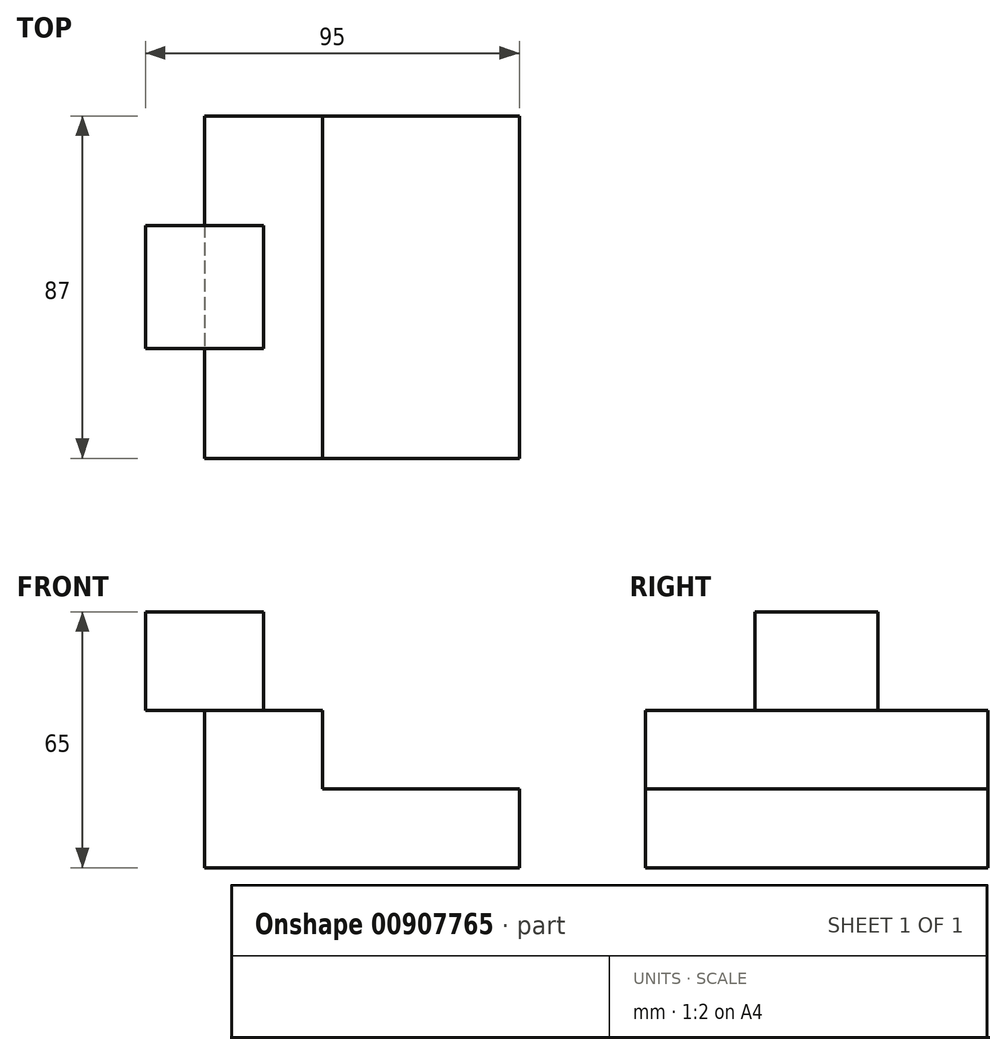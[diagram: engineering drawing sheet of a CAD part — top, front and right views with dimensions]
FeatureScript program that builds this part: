
annotation { "Feature Type Name" : "Feature", "Feature Type Description" : "" }
export const myFeature = defineFeature(function(context is Context, id is Id, definition is map)
    precondition{}
    {
        {
            var Q0;
            Q0=qCreatedBy(makeId("Front.planeOp"),FACE);
            var sketch = newSketch(context, id + "F0", { "sketchPlane" : qUnion([Q0])});
            skLineSegment(sketch, "E0.top", {"start": v(0, 40) * mm, "end": v(30, 40) * mm});
            skLineSegment(sketch, "E0.left", {"start": v(0, 0) * mm, "end": v(0, 40) * mm});
            skLineSegment(sketch, "E0.right", {"start": v(30, 20) * mm, "end": v(30, 40) * mm});
            skLineSegment(sketch, "E1.bottom", {"start": v(30, 20) * mm, "end": v(80, 20) * mm});
            skLineSegment(sketch, "E1.right", {"start": v(80, 20) * mm, "end": v(80, 0) * mm});
            skLineSegment(sketch, "E2", {"start": v(80, 0) * mm, "end": v(0, 0) * mm});
            skSolve(sketch);
        }
        {
            var Q0;
            Q0 = qSketchRegion(id + "F0", true);
            extrude(context, id + "F1", {"entities" : qUnion([Q0]), "oppositeDirection" : true, "depth" : 87 * mm, "offsetDistance" : 25 * mm});
        }
        {
            var Q0;
            Q0=makeQuery(id+"F1.opExtrude","SWEPT_FACE",FACE,{"disambiguationData":[OSD([sQuery(id+"F0.wireOp",EDGE,"E1.bottom")])]});
            var sketch = newSketch(context, id + "F2", { "sketchPlane" : qUnion([Q0])});
            skPoint(sketch, "E3", {"position": v(55, 43.5) * mm});
            skPoint(sketch, "E3.positionSnap0", {"position": v(55, 0) * mm});
            skPoint(sketch, "E3.positionSnap1", {"position": v(30, 43.5) * mm});
            skSolve(sketch);
        }
        {
            var Q0;
            Q0=makeQuery(id+"F1.opExtrude","SWEPT_FACE",FACE,{"disambiguationData":[OSD([sQuery(id+"F0.wireOp",EDGE,"E0.top")])]});
            var sketch = newSketch(context, id + "F3", { "sketchPlane" : qUnion([Q0])});
            skLineSegment(sketch, "E4.bottom", {"start": v(15, 27.88) * mm, "end": v(-15, 27.88) * mm});
            skLineSegment(sketch, "E4.top", {"start": v(15, 59.12) * mm, "end": v(-15, 59.12) * mm});
            skLineSegment(sketch, "E4.left", {"start": v(15, 27.88) * mm, "end": v(15, 59.12) * mm});
            skLineSegment(sketch, "E4.right", {"start": v(-15, 27.88) * mm, "end": v(-15, 59.12) * mm});
            skPoint(sketch, "E4.middle", {"position": v(-40.2, 70.7) * mm});
            skPoint(sketch, "E4.cornerSnap0", {"position": v(15, 0) * mm});
            skPoint(sketch, "E5.left.end.orphan", {"position": v(-55.2, 55.07) * mm});
            skPoint(sketch, "E5.bottom.start.orphan", {"position": v(-55.2, 86.32) * mm});
            skPoint(sketch, "E5.right.end.orphan", {"position": v(-25.2, 55.07) * mm});
            skPoint(sketch, "E5.right.start.orphan", {"position": v(-25.2, 86.32) * mm});
            skSolve(sketch);
        }
        {
            var Q0;
            Q0 = qSketchRegion(id + "F3", true);
            extrude(context, id + "F4", {"entities" : qUnion([Q0]), "operationType" : NewBodyOperationType.ADD, "depth" : 25 * mm, "offsetDistance" : 25 * mm});
        }
    });
